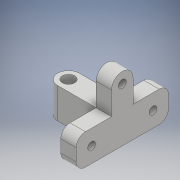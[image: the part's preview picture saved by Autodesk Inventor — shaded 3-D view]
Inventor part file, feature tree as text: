
AUTODESK INVENTOR PART (.ipt)
format: ipt  version: 2017 (Build 210142000, 142)  size: 152,576 bytes
history: native  units: mm
features: extrude x3, sketch x3, fillet x1
ambient origin geometry x8: Origin, YZ Plane, XZ Plane, XY Plane, X Axis, Y Axis, Z Axis, Center Point
bodies: Solid1 (feature_tree)
feature tree (7):
  extrude  "Extrusion1"  Depth=25.0mm
  extrude  "Extrusion2"  Depth=10.0mm
  fillet  "Fillet1"  Radius=7.0mm
  extrude  "Extrusion3"  Depth=10.0mm
  sketch  "Sketch1"  dims[d0=8.0mm d1=25.0mm]
  sketch  "Sketch2"  dims[d2=60.0mm d3=10.0mm d4=7.0mm]
  sketch  "Sketch3"  dims[d5=20.0mm d6=0.0mm d7=5.0mm d8=10.0mm d9=20.0mm d10=0.0mm d11=6.0mm d12=5.0mm d13=7.0mm d14=15.0mm d15=10.0mm d16=0.0mm]
